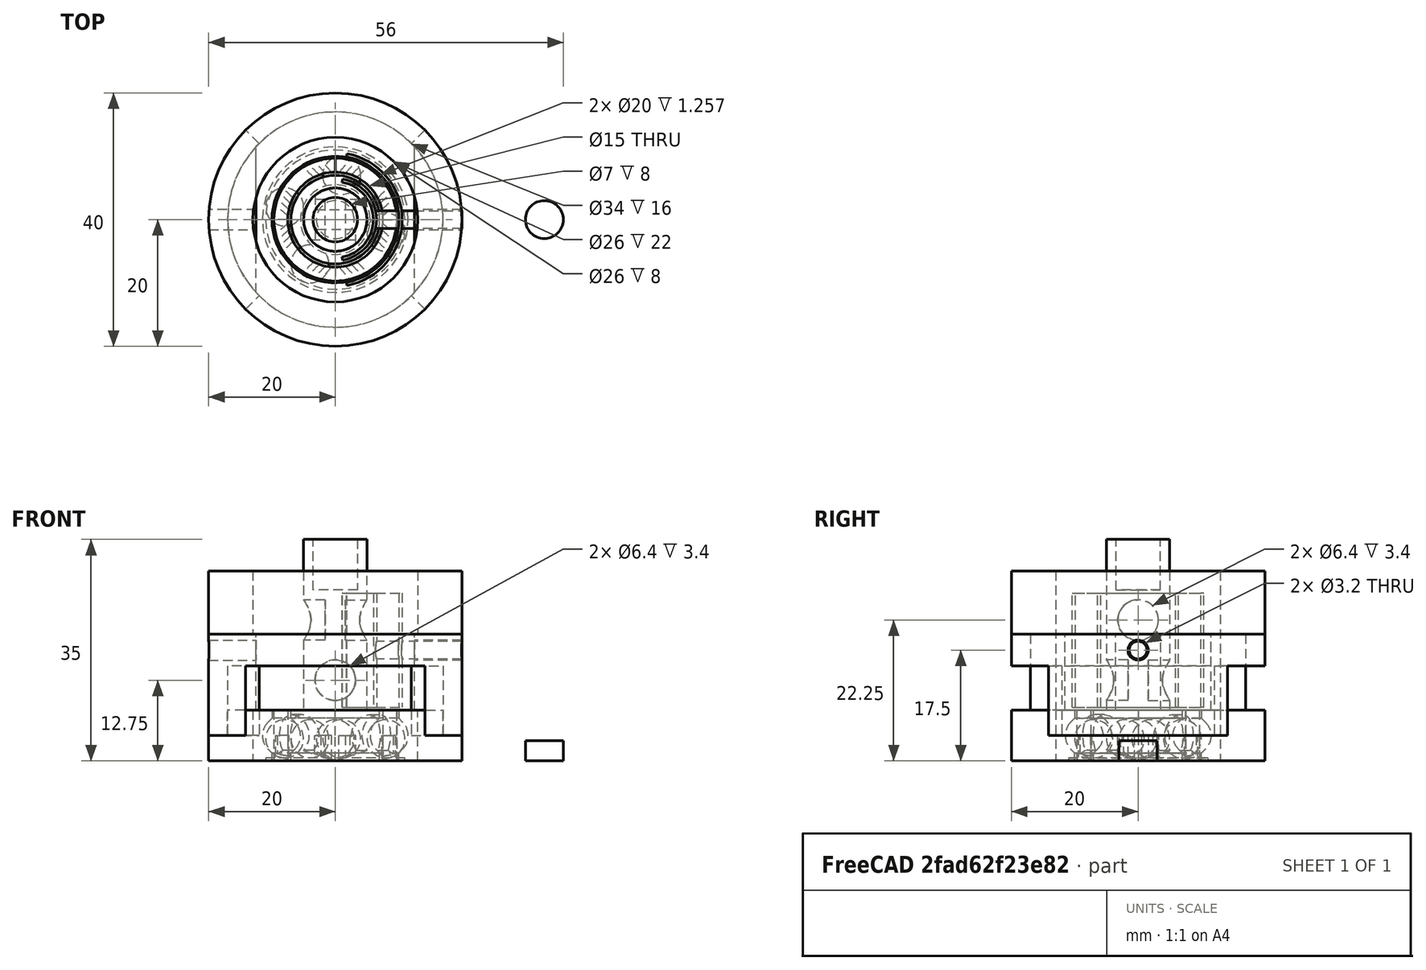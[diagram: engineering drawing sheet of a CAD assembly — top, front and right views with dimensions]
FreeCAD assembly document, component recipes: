
FREECAD ASSEMBLY — COMPONENT RECIPES ("laser")

This assembly document has 11 components, labeled P0..P10 below (a component is one placed body or linked part). 6 of them carry a construction recipe — the FreeCAD feature program that regenerates the part from scratch, quoted from this document or its linked companion documents; the rest are supplied as boundary geometry only. No exploded tour is included for this assembly.
COMPONENT P0 — recipe-attached ("bearing_body001", modeled in this document).
Construction recipe (the document's own serialized feature program — sketch geometry with constraints, then the solid features built on it; lengths are millimeters unless a unit is written):

FEATURE [PartDesign::SubShapeBinder] Binder
  BindCopyOnChange = 0
  BindMode = 0
  ClaimChildren = false
  Context = -> Body007 [Binder.]
  Fuse = false
  MakeFace = true
  OffsetFill = false
  OffsetIntersection = false
  OffsetJoinType = 0
  OffsetOpenResult = false
  PartialLoad = false
  Refine = true
  Relative = true
  Support = -> [Body[Revolution.]]
  _Version = 2
FEATURE [Sketcher::SketchObject] Sketch035
  ArcFitTolerance = 1e-06
  AttachmentSupport = -> [XZ_Plane008]
  ExternalGeometry = -> [Binder]
  ExternalTypes = [0]
  FullyConstrained = true
  MakeInternals = false
  MapMode = 5
  Placement = pos=(0,0,0) rot=(1,0,0;1.5708rad)
  expr: Constraints[25] = Spreadsheet.bearing_ball_radius
  expr: Constraints[6] = Spreadsheet.bearing_ball_radius + Spreadsheet.bearing_ball_radius_extra_play / 2
  sketch-geometry (17):
    g0: LineSegment [constr] StartX=8.5 StartY=8 StartZ=0 EndX=8.5 EndY=0 EndZ=0
    g1: LineSegment StartX=10 StartY=8 StartZ=0 EndX=10 EndY=6.74264 EndZ=0
    g2: LineSegment [constr] StartX=7 StartY=6.74264 StartZ=0 EndX=10 EndY=6.74264 EndZ=0
    g3: GeomPoint [constr] X=8.5 Y=4 Z=0
    g4: ArcOfCircle CenterX=8.5 CenterY=4 CenterZ=0 NormalX=0 NormalY=0 NormalZ=1 AngleXU=0 Radius=3 StartAngle=0 EndAngle=0.785398
    g5: LineSegment StartX=10.6213 StartY=6.12132 StartZ=0 EndX=10 EndY=6.74264 EndZ=0
    g6: ArcOfCircle CenterX=8.5 CenterY=4 CenterZ=0 NormalX=0 NormalY=0 NormalZ=1 AngleXU=0 Radius=3 StartAngle=5.49779 EndAngle=6.28319
    g7: LineSegment StartX=10 StartY=0 StartZ=0 EndX=10 EndY=1.25736 EndZ=0
    g8: LineSegment StartX=10.6213 StartY=1.87868 StartZ=0 EndX=10 EndY=1.25736 EndZ=0
    g9: LineSegment [constr] StartX=8.5 StartY=4 StartZ=0 EndX=11.5 EndY=4 EndZ=0
    g10: LineSegment StartX=10 StartY=8 StartZ=0 EndX=13 EndY=8 EndZ=0
    g11: LineSegment [constr] StartX=7 StartY=8 StartZ=0 EndX=10 EndY=8 EndZ=0
    g12: LineSegment [constr] StartX=7 StartY=1.25736 StartZ=0 EndX=10 EndY=1.25736 EndZ=0
    g13: LineSegment StartX=13 StartY=8 StartZ=0 EndX=13 EndY=0 EndZ=0
    g14: LineSegment StartX=13 StartY=0 StartZ=0 EndX=10 EndY=0 EndZ=0
    g15: LineSegment [constr] StartX=0 StartY=0 StartZ=0 EndX=13 EndY=0 EndZ=0
    g16: LineSegment [constr] StartX=10 StartY=6.74264 StartZ=0 EndX=10 EndY=1.25736 EndZ=0
  constraints (43):
    c: Vertical(g0)
    c: Vertical(g1)
    c: Coincident(g2,g1)
    c: Horizontal(g2)
    c: Symmetric(g0,g0,g3)
    c: PointOnObject(g0,g-1)
    c: Radius(g4) = 3
    c: Angle(g4) = 0.785398
    c: Coincident(g4,g3)
    c: Coincident(g5,g1)
    c: Angle(g6) = 0.785398
    c: Coincident(g6,g3)
    c: Coincident(g6,g4)
    c: PointOnObject(g7,g-1)
    c: Coincident(g8,g7)
    c: Vertical(g7)
    c: Coincident(g9,g3)
    c: Coincident(g9,g4)
    c: Horizontal(g9)
    c: Horizontal(g10)
    c: Tangent(g5,g4) = -1.5708
    c: Tangent(g8,g6) = 1.5708
    c: Coincident(g1,g10)
    c: Coincident(g11,g1)
    c: Horizontal(g11)
    c: Distance(g11) = 3
    c: Coincident(g12,g7)
    c: Horizontal(g12)
    c: Equal(g12,g11)
    c: Coincident(g13,g10)
    c: PointOnObject(g13,g-1)
    c: Vertical(g13)
    c: Coincident(g14,g13)
    c: Coincident(g14,g7)
    c: Coincident(g15,g-1)
    c: Coincident(g15,g13)
    c: DistanceX(g15,g15) = 13
    c: Coincident(g16,g1)
    c: Coincident(g16,g7)
    c: Vertical(g16)
    c: PointOnObject(g0,g11)
    c: Coincident(g11,g-4)
    c: Coincident(g2,g-5)
FEATURE [PartDesign::Revolution] Revolution001
  Angle = 360
  Angle2 = 60
  Axis = (0,2e-16,1)
  Base = (0,0,0)
  FuseOrder = 1
  Placement = pos=(0,0,0) rot=(1,0,0;1.5708rad)
  Profile = -> Sketch035
  ReferenceAxis = -> Sketch035 [V_Axis]
  Refine = true
  Reversed = true
  Suppressed = false
  Type = 0
FEATURE [PartDesign::Body] Body007  label="bearing_body"
  AllowCompound = false
  Group = -> [Sketch035,Revolution001,Binder]
  Origin = -> Origin008
  Tip = -> Revolution001
COMPONENT P1 — recipe-attached ("bearing_holder001", modeled in this document).
Construction recipe (the document's own serialized feature program — sketch geometry with constraints, then the solid features built on it; lengths are millimeters unless a unit is written):

FEATURE [Sketcher::SketchObject] Sketch041
  ArcFitTolerance = 1e-06
  AttachmentSupport = -> [XY_Plane012]
  ExternalTypes = [0]
  FullyConstrained = true
  MakeInternals = false
  MapMode = 5
  sketch-geometry (2):
    g0: Circle CenterX=0 CenterY=0 CenterZ=0 NormalX=0 NormalY=0 NormalZ=1 AngleXU=0 Radius=13
    g1: Circle CenterX=0 CenterY=0 CenterZ=0 NormalX=0 NormalY=0 NormalZ=1 AngleXU=0 Radius=20
  constraints (4):
    c: Diameter(g0) = 26
    c: Coincident(g0,g-1)
    c: Diameter(g1) = 40
    c: Coincident(g1,g0)
FEATURE [PartDesign::Pad] Pad018
  Direction = (0,0,1)
  Length = 8
  Length2 = 10
  Profile = -> Sketch041
  ReferenceAxis = -> Sketch041 [N_Axis]
  Refine = true
  SideType = 0
  Suppressed = false
  Type = 0
  Type2 = 0
FEATURE [Sketcher::SketchObject] Sketch042
  ArcFitTolerance = 1e-06
  AttachmentSupport = -> [Pad018]
  ExternalGeometry = -> [Pad018]
  ExternalTypes = [0]
  FullyConstrained = true
  MakeInternals = false
  MapMode = 5
  Placement = pos=(0,0,8) rot=(0,0,1;0rad)
  sketch-geometry (10):
    g0: ArcOfCircle CenterX=0 CenterY=0 CenterZ=0 NormalX=0 NormalY=0 NormalZ=1 AngleXU=0 Radius=20 StartAngle=5.49779 EndAngle=7.06858
    g1: ArcOfCircle CenterX=0 CenterY=0 CenterZ=0 NormalX=0 NormalY=0 NormalZ=1 AngleXU=0 Radius=17 StartAngle=5.49779 EndAngle=7.06858
    g2: LineSegment StartX=12.0208 StartY=-12.0208 StartZ=0 EndX=14.1421 EndY=-14.1421 EndZ=0
    g3: LineSegment StartX=12.0208 StartY=12.0208 StartZ=0 EndX=14.1421 EndY=14.1421 EndZ=0
    g4: LineSegment [constr] StartX=0 StartY=0 StartZ=0 EndX=12.0208 EndY=12.0208 EndZ=0
    g5: ArcOfCircle CenterX=0 CenterY=0 CenterZ=0 NormalX=0 NormalY=0 NormalZ=1 AngleXU=0 Radius=20 StartAngle=2.35619 EndAngle=3.92699
    g6: ArcOfCircle CenterX=0 CenterY=0 CenterZ=0 NormalX=0 NormalY=0 NormalZ=1 AngleXU=0 Radius=17 StartAngle=2.35619 EndAngle=3.92699
    g7: LineSegment [constr] StartX=0 StartY=0 StartZ=0 EndX=-12.0208 EndY=-12.0208 EndZ=0
    g8: LineSegment StartX=-12.0208 StartY=12.0208 StartZ=0 EndX=-14.1421 EndY=14.1421 EndZ=0
    g9: LineSegment StartX=-12.0208 StartY=-12.0208 StartZ=0 EndX=-14.1421 EndY=-14.1421 EndZ=0
  constraints (28):
    c: Angle(g0) = 1.5708
    c: Coincident(g0,g-1)
    c: PointOnObject(g0,g-3)
    c: Angle(g1) = 1.5708
    c: Coincident(g1,g0)
    c: Coincident(g2,g1)
    c: Coincident(g2,g0)
    c: Coincident(g3,g1)
    c: Coincident(g3,g0)
    c: Distance(g3) = 3
    c: Coincident(g4,g0)
    c: Coincident(g4,g1)
    c: Parallel(g3,g4)
    c: Angle(g-1,g4) = 0.785398
    c: Angle(g5) = 1.5708
    c: Coincident(g5,g0)
    c: PointOnObject(g5,g-3)
    c: Angle(g6) = 1.5708
    c: Coincident(g6,g0)
    c: Coincident(g7,g0)
    c: Coincident(g7,g6)
    c: Angle(g7,g-1) = 2.35619
    c: Coincident(g8,g6)
    c: Coincident(g8,g5)
    c: Coincident(g9,g6)
    c: Coincident(g9,g5)
    c: Distance(g8) = 3
    c: Parallel(g9,g7)
FEATURE [PartDesign::Pocket] Pocket018
  BaseFeature = -> Pad018
  Direction = (0,0,-1)
  Length = 4
  Length2 = 5
  Profile = -> Sketch042
  ReferenceAxis = -> Sketch042 [N_Axis]
  Refine = true
  SideType = 0
  Suppressed = false
  Type = 0
  Type2 = 0
FEATURE [PartDesign::Body] Body011  label="bearing_holder"
  AllowCompound = false
  Group = -> [Sketch041,Pad018,Sketch042,Pocket018]
  Origin = -> Origin012
  Tip = -> Pocket018
COMPONENT P2 — recipe-attached ("coil001", modeled in this document).
Construction recipe (the document's own serialized feature program — sketch geometry with constraints, then the solid features built on it; lengths are millimeters unless a unit is written):

FEATURE [Sketcher::SketchObject] Sketch046
  ArcFitTolerance = 1e-06
  AttachmentOffset = pos=(0,0,8.5) rot=(0,0,1;0rad)
  AttachmentSupport = -> [XY_Plane014]
  ExternalTypes = [0]
  FullyConstrained = true
  MakeInternals = false
  MapMode = 5
  Placement = pos=(0,0,8.5) rot=(0,0,1;0rad)
  sketch-geometry (11):
    g0: GeomPoint X=5 Y=0 Z=0
    g1: GeomPoint X=6 Y=0 Z=0
    g2: LineSegment [constr] StartX=5 StartY=0 StartZ=0 EndX=6 EndY=0 EndZ=0
    g3: LineSegment [constr] StartX=1.04189 StartY=5.90885 StartZ=0 EndX=1.12871 EndY=6.40125 EndZ=0
    g4: ArcOfCircle CenterX=0 CenterY=0 CenterZ=0 NormalX=0 NormalY=0 NormalZ=1 AngleXU=0 Radius=6 StartAngle=4.88692 EndAngle=7.67945
    g5: LineSegment [constr] StartX=1.04189 StartY=-5.90885 StartZ=0 EndX=0 EndY=0 EndZ=0
    g6: LineSegment [constr] StartX=0 StartY=0 StartZ=0 EndX=1.04189 EndY=5.90885 EndZ=0
    g7: ArcOfCircle CenterX=0 CenterY=0 CenterZ=0 NormalX=0 NormalY=0 NormalZ=1 AngleXU=0 Radius=6.5 StartAngle=4.88692 EndAngle=7.67945
    g8: LineSegment [constr] StartX=1.12871 StartY=-6.40125 StartZ=0 EndX=1.04189 EndY=-5.90885 EndZ=0
    g9: LineSegment StartX=1.12871 StartY=-6.40125 StartZ=0 EndX=1.04189 EndY=-5.90885 EndZ=0
    g10: LineSegment StartX=1.12871 StartY=6.40125 StartZ=0 EndX=1.04189 EndY=5.90885 EndZ=0
  constraints (26):
    c: PointOnObject(g0,g-3)
    c: PointOnObject(g1,g4)
    c: PointOnObject(g0,g-1)
    c: PointOnObject(g1,g-1)
    c: Coincident(g2,g0)
    c: Coincident(g2,g1)
    c: Distance(g2,g2) = 1
    c: Coincident(g5,g-1)
    c: Angle(g-1,g6) = 1.39626
    c: Angle(g5,g-1) = 1.39626
    c: Coincident(g6,g4)
    c: Coincident(g4,g5)
    c: Coincident(g7,g4)
    c: Parallel(g3,g6)
    c: Coincident(g3,g7)
    c: Coincident(g6,g4)
    c: Coincident(g3,g4)
    c: Distance(g3,g3) = 0.5
    c: Coincident(g8,g7)
    c: Coincident(g8,g4)
    c: Parallel(g8,g5)
    c: Coincident(g4,g5)
    c: Coincident(g9,g7)
    c: Coincident(g9,g4)
    c: Coincident(g10,g3)
    c: Coincident(g10,g3)
FEATURE [PartDesign::SubShapeBinder] Binder011
  BindCopyOnChange = 0
  BindMode = 0
  ClaimChildren = false
  Context = -> Body013 [Binder011.]
  Fuse = false
  MakeFace = true
  OffsetFill = false
  OffsetIntersection = false
  OffsetJoinType = 0
  OffsetOpenResult = false
  PartialLoad = false
  Refine = true
  Relative = true
  Support = -> [Body]
  _Version = 2
FEATURE [PartDesign::Pad] Pad023
  Direction = (0,0,1)
  Length = 18
  Length2 = 10
  Profile = -> Sketch046
  ReferenceAxis = -> Sketch046 [N_Axis]
  Refine = true
  SideType = 0
  Suppressed = false
  Type = 0
  Type2 = 0
FEATURE [Sketcher::SketchObject] Sketch047
  ArcFitTolerance = 1e-06
  AttachmentSupport = -> [Pad023]
  ExternalGeometry = -> [Pad023]
  ExternalTypes = [0]
  FullyConstrained = true
  MakeInternals = false
  MapMode = 5
  Placement = pos=(0,0,26.5) rot=(0,0,1;0rad)
  sketch-geometry (3):
    g0: GeomPoint X=6.5 Y=0 Z=0
    g1: GeomPoint X=6 Y=0 Z=0
    g2: LineSegment StartX=6 StartY=0 StartZ=0 EndX=6.5 EndY=0 EndZ=0
  constraints (6):
    c: PointOnObject(g0,g-4)
    c: PointOnObject(g1,g-3)
    c: Coincident(g2,g1)
    c: Coincident(g2,g0)
    c: Horizontal(g2)
    c: PointOnObject(g0,g-1)
FEATURE [PartDesign::Plane] DatumPlane006
  AttachmentOffset = pos=(0,0,0) rot=(0,1,0;3.14159rad)
  AttachmentSupport = -> [Sketch047]
  Length = 60.1489
  MapMode = 7
  Placement = pos=(6.5,0,26.5) rot=(0.57735,0.57735,0.57735;2.0944rad)
  ResizeMode = 0
  Width = 61.6489
FEATURE [Sketcher::SketchObject] Sketch049
  ArcFitTolerance = 1e-06
  AttachmentOffset = pos=(0,0,-0.5) rot=(0,0,1;0rad)
  AttachmentSupport = -> [DatumPlane006]
  ExternalGeometry = -> [Pad023]
  ExternalTypes = [0]
  FullyConstrained = true
  MakeInternals = false
  MapMode = 5
  Placement = pos=(6,0,26.5) rot=(0.57735,0.57735,0.57735;2.0944rad)
  sketch-geometry (4):
    g0: LineSegment [constr] StartX=-6.40125 StartY=0 StartZ=0 EndX=6.40125 EndY=-18 EndZ=0
    g1: LineSegment [constr] StartX=-6.40125 StartY=-18 StartZ=0 EndX=6.40125 EndY=0 EndZ=0
    g2: GeomPoint [constr] X=0 Y=-9 Z=0
    g3: Circle CenterX=0 CenterY=-9 CenterZ=0 NormalX=0 NormalY=0 NormalZ=1 AngleXU=0 Radius=1.4
  constraints (7):
    c: Coincident(g0,g-5)
    c: Coincident(g0,g-6)
    c: Coincident(g1,g-6)
    c: Coincident(g1,g-5)
    c: Symmetric(g0,g0,g2)
    c: Diameter(g3) = 2.8
    c: Coincident(g3,g2)
FEATURE [PartDesign::Pad] Pad024
  BaseFeature = -> Pad023
  Direction = (1,0,0)
  Length = 14
  Length2 = 10
  Profile = -> Sketch049
  ReferenceAxis = -> Sketch049 [N_Axis]
  Refine = true
  SideType = 0
  Suppressed = false
  Type = 0
  Type2 = 0
FEATURE [Sketcher::SketchObject] Sketch050
  ArcFitTolerance = 1e-06
  AttachmentOffset = pos=(0,0,8.5) rot=(0,0,1;0rad)
  AttachmentSupport = -> [XY_Plane014]
  ExternalGeometry = -> [Pad023]
  ExternalTypes = [0]
  FullyConstrained = true
  MakeInternals = false
  MapMode = 5
  Placement = pos=(0,0,8.5) rot=(0,0,1;0rad)
  sketch-geometry (7):
    g0: ArcOfCircle CenterX=0 CenterY=0 CenterZ=0 NormalX=0 NormalY=0 NormalZ=1 AngleXU=0 Radius=10.054 StartAngle=4.88692 EndAngle=7.67945
    g1: LineSegment [constr] StartX=1.83268 StartY=-10.3937 StartZ=0 EndX=1.74586 EndY=-9.90125 EndZ=0
    g2: LineSegment StartX=1.83268 StartY=10.3937 StartZ=0 EndX=1.74586 EndY=9.90125 EndZ=0
    g3: LineSegment StartX=1.83268 StartY=-10.3937 StartZ=0 EndX=1.74586 EndY=-9.90125 EndZ=0
    g4: ArcOfCircle CenterX=0 CenterY=0 CenterZ=0 NormalX=0 NormalY=0 NormalZ=1 AngleXU=0 Radius=10.554 StartAngle=4.88692 EndAngle=7.67945
    g5: LineSegment [constr] StartX=1.74586 StartY=-9.90125 StartZ=0 EndX=1.12871 EndY=-6.40125 EndZ=0
    g6: LineSegment [constr] StartX=1.12871 StartY=6.40125 StartZ=0 EndX=1.74586 EndY=9.90125 EndZ=0
  constraints (18):
    c: Coincident(g1,g0)
    c: Coincident(g2,g0)
    c: Coincident(g3,g0)
    c: Coincident(g0,g-1)
    c: Coincident(g4,g0)
    c: Coincident(g4,g3)
    c: Coincident(g4,g2)
    c: Coincident(g1,g3)
    c: Parallel(g2,g-5)
    c: Parallel(g3,g-6)
    c: Coincident(g5,g0)
    c: Coincident(g5,g-6)
    c: Parallel(g-6,g5)
    c: Coincident(g6,g-5)
    c: Coincident(g6,g0)
    c: Parallel(g6,g-5)
    c: Distance(g2,g2) = 0.5
    c: DistanceY(g6,g6) = 3.5
FEATURE [PartDesign::Pad] Pad025
  BaseFeature = -> Pad024
  Direction = (0,0,1)
  Length = 18
  Length2 = 10
  Profile = -> Sketch050
  ReferenceAxis = -> Sketch050 [N_Axis]
  Refine = true
  SideType = 0
  Suppressed = false
  Type = 0
  Type2 = 0
FEATURE [PartDesign::Body] Body013  label="coil"
  AllowCompound = false
  Group = -> [Sketch046,Binder011,Pad023,Sketch047,DatumPlane006,Sketch049,Pad024,Sketch050,Pad025]
  Origin = -> Origin014
  Tip = -> Pad025
COMPONENT P3 — same part as P2; its construction recipe is shown at P2.
COMPONENT P4 — recipe-attached ("coil_frame001", modeled in this document).
Construction recipe (the document's own serialized feature program — sketch geometry with constraints, then the solid features built on it; lengths are millimeters unless a unit is written):

FEATURE [PartDesign::SubShapeBinder] Binder009
  BindCopyOnChange = 0
  BindMode = 0
  ClaimChildren = false
  Context = -> Body012 [Binder009.]
  Fuse = false
  MakeFace = true
  OffsetFill = false
  OffsetIntersection = false
  OffsetJoinType = 0
  OffsetOpenResult = false
  PartialLoad = false
  Refine = true
  Relative = true
  Support = -> [Body011]
  _Version = 2
FEATURE [Sketcher::SketchObject] Sketch044
  ArcFitTolerance = 1e-06
  AttachmentOffset = pos=(0,0,15) rot=(0,0,1;0rad)
  AttachmentSupport = -> [Binder009]
  ExternalTypes = [0]
  FullyConstrained = true
  MakeInternals = false
  MapMode = 5
  Placement = pos=(0,0,15) rot=(0,0,1;3.14159rad)
  sketch-geometry (15):
    g0: Circle CenterX=0 CenterY=0 CenterZ=0 NormalX=0 NormalY=0 NormalZ=1 AngleXU=0 Radius=20
    g1: Circle [constr] CenterX=0 CenterY=0 CenterZ=0 NormalX=0 NormalY=0 NormalZ=1 AngleXU=0 Radius=6.5
    g2: GeomPoint [constr] X=5 Y=0 Z=0
    g3: LineSegment [constr] StartX=6.5 StartY=0 StartZ=0 EndX=5 EndY=0 EndZ=0
    g4: LineSegment StartX=12.5 StartY=11.5217 StartZ=0 EndX=12.5 EndY=-11.5217 EndZ=0
    g5: ArcOfCircle CenterX=-1.6699e-12 CenterY=-6e-16 CenterZ=0 NormalX=0 NormalY=0 NormalZ=1 AngleXU=0 Radius=17 StartAngle=0.744696 EndAngle=2.3969
    g6: GeomPoint X=12.5 Y=0 Z=0
    g7: LineSegment StartX=-12.5 StartY=11.5217 StartZ=0 EndX=-12.5 EndY=-11.5217 EndZ=0
    g8: ArcOfCircle CenterX=0 CenterY=0 CenterZ=0 NormalX=0 NormalY=0 NormalZ=1 AngleXU=0 Radius=17 StartAngle=3.88629 EndAngle=5.53849
    g9: GeomPoint X=-12.5 Y=0 Z=0
    g10: GeomPoint X=-6.5 Y=0 Z=0
    g11: LineSegment [constr] StartX=-12.5 StartY=0 StartZ=0 EndX=-6.5 EndY=0 EndZ=0
    g12: LineSegment [constr] StartX=12.5 StartY=0 StartZ=0 EndX=6.5 EndY=0 EndZ=0
    g13: Circle [constr] CenterX=-1.6699e-12 CenterY=-6e-16 CenterZ=0 NormalX=0 NormalY=0 NormalZ=1 AngleXU=0 Radius=17
    g14: GeomPoint [constr] X=-12.0208 Y=-12.0208 Z=0
  constraints (35):
    c: Coincident(g0,g-1)
    c: Coincident(g1,g0)
    c: PointOnObject(g2,g-5)
    c: PointOnObject(g3,g1)
    c: Coincident(g3,g2)
    c: PointOnObject(g2,g-1)
    c: PointOnObject(g3,g-1)
    c: Distance(g3,g3) = 1.5
    c: PointOnObject(g4,g5)
    c: PointOnObject(g-3,g0)
    c: Coincident(g8,g4)
    c: PointOnObject(g5,g4)
    c: Symmetric(g4,g4,g6)
    c: PointOnObject(g6,g-1)
    c: PointOnObject(g9,g7)
    c: PointOnObject(g10,g1)
    c: PointOnObject(g10,g-1)
    c: PointOnObject(g9,g-1)
    c: Coincident(g11,g9)
    c: Coincident(g11,g10)
    c: Coincident(g12,g6)
    c: Coincident(g12,g3)
    c: Equal(g11,g12)
    c: Coincident(g7,g5)
    c: Coincident(g7,g8)
    c: Vertical(g7)
    c: Distance(g12,g12) = 6
    c: Vertical(g4)
    c: Equal(g4,g7)
    c: Coincident(g8,g0)
    c: Coincident(g13,g5)
    c: PointOnObject(g-4,g13)
    c: PointOnObject(g5,g13)
    c: PointOnObject(g14,g13)
    c: Coincident(g14,g-4)
FEATURE [PartDesign::Pad] Pad021
  Direction = (0,0,1)
  Length = 5
  Length2 = 10
  Profile = -> Sketch044
  ReferenceAxis = -> Sketch044 [N_Axis]
  Refine = true
  SideType = 0
  Suppressed = false
  Type = 0
  Type2 = 0
FEATURE [Sketcher::SketchObject] Sketch045
  ArcFitTolerance = 1e-06
  AttachmentSupport = -> [Pad021]
  ExternalGeometry = -> [Binder009]
  ExternalTypes = [0]
  FullyConstrained = true
  MakeInternals = false
  MapMode = 5
  Placement = pos=(0,0,15) rot=(1,0,0;3.14159rad)
  sketch-geometry (12):
    g0: ArcOfCircle CenterX=0 CenterY=0 CenterZ=0 NormalX=0 NormalY=0 NormalZ=1 AngleXU=0 Radius=20 StartAngle=2.35619 EndAngle=3.92699
    g1: ArcOfCircle CenterX=0 CenterY=0 CenterZ=0 NormalX=0 NormalY=0 NormalZ=1 AngleXU=0 Radius=17 StartAngle=2.35619 EndAngle=3.92699
    g2: ArcOfCircle CenterX=0 CenterY=0 CenterZ=0 NormalX=0 NormalY=0 NormalZ=1 AngleXU=0 Radius=20 StartAngle=5.49779 EndAngle=7.06858
    g3: ArcOfCircle CenterX=0 CenterY=0 CenterZ=0 NormalX=0 NormalY=0 NormalZ=1 AngleXU=0 Radius=17 StartAngle=5.49779 EndAngle=7.06858
    g4: LineSegment StartX=-14.1421 StartY=-14.1421 StartZ=0 EndX=-12.0208 EndY=-12.0208 EndZ=0
    g5: LineSegment StartX=-14.1421 StartY=14.1421 StartZ=0 EndX=-12.0208 EndY=12.0208 EndZ=0
    g6: LineSegment StartX=14.1421 StartY=-14.1421 StartZ=0 EndX=12.0208 EndY=-12.0208 EndZ=0
    g7: LineSegment StartX=14.1421 StartY=14.1421 StartZ=0 EndX=12.0208 EndY=12.0208 EndZ=0
    g8: LineSegment [constr] StartX=0 StartY=0 StartZ=0 EndX=12.0208 EndY=-12.0208 EndZ=0
    g9: LineSegment [constr] StartX=-12.0208 StartY=-12.0208 StartZ=0 EndX=0 EndY=0 EndZ=0
    g10: LineSegment [constr] StartX=12.0208 StartY=-12.0208 StartZ=0 EndX=14.1421 EndY=-14.1421 EndZ=0
    g11: LineSegment [constr] StartX=-14.1421 StartY=-14.1421 StartZ=0 EndX=-12.0208 EndY=-12.0208 EndZ=0
  constraints (28):
    c: Coincident(g0,g-1)
    c: Coincident(g0,g-4)
    c: Coincident(g1,g0)
    c: Coincident(g1,g-3)
    c: Coincident(g2,g0)
    c: Coincident(g2,g-7)
    c: Coincident(g3,g0)
    c: Coincident(g3,g-5)
    c: Coincident(g4,g0)
    c: Coincident(g4,g1)
    c: Coincident(g5,g0)
    c: Coincident(g5,g1)
    c: Coincident(g6,g2)
    c: Coincident(g6,g3)
    c: Coincident(g7,g2)
    c: Coincident(g7,g3)
    c: Coincident(g8,g0)
    c: Coincident(g8,g3)
    c: Coincident(g9,g1)
    c: Coincident(g9,g0)
    c: Parallel(g4,g9)
    c: Parallel(g8,g6)
    c: Coincident(g10,g-5)
    c: Coincident(g10,g-6)
    c: Parallel(g6,g10)
    c: Coincident(g11,g-4)
    c: Coincident(g11,g-3)
    c: Parallel(g4,g11)
FEATURE [PartDesign::Pad] Pad022
  BaseFeature = -> Pad021
  Direction = (0,0,-1)
  Length = 10
  Length2 = 10
  Profile = -> Sketch045
  ReferenceAxis = -> Sketch045 [N_Axis]
  Refine = true
  SideType = 0
  Suppressed = false
  Type = 3
  Type2 = 0
  UpToFace = -> Binder009 [Face7]
FEATURE [PartDesign::SubShapeBinder] Binder010
  BindCopyOnChange = 0
  BindMode = 0
  ClaimChildren = false
  Context = -> Body012 [Binder010.]
  Fuse = false
  MakeFace = true
  OffsetFill = false
  OffsetIntersection = false
  OffsetJoinType = 0
  OffsetOpenResult = false
  PartialLoad = false
  Refine = true
  Relative = true
  Support = -> [Body]
  _Version = 2
FEATURE [PartDesign::SubShapeBinder] Binder012
  BindCopyOnChange = 0
  BindMode = 0
  ClaimChildren = false
  Context = -> Body012 [Binder012.]
  Fuse = false
  MakeFace = true
  OffsetFill = false
  OffsetIntersection = false
  OffsetJoinType = 0
  OffsetOpenResult = false
  PartialLoad = false
  Refine = true
  Relative = true
  Support = -> [Body013]
  _Version = 2
FEATURE [Sketcher::SketchObject] Sketch051
  ArcFitTolerance = 1e-06
  AttachmentSupport = -> [Pad021]
  ExternalGeometry = -> [Binder012]
  ExternalTypes = [0]
  FullyConstrained = true
  MakeInternals = false
  MapMode = 5
  Placement = pos=(-12.5,0,0) rot=(0.57735,0.57735,0.57735;2.0944rad)
  sketch-geometry (3):
    g0: Circle CenterX=-5e-16 CenterY=17.5 CenterZ=0 NormalX=0 NormalY=0 NormalZ=1 AngleXU=0 Radius=1.6
    g1: GeomPoint [constr] X=0 Y=19.1 Z=0
    g2: GeomPoint [constr] X=0 Y=18.9 Z=0
  constraints (6):
    c: Coincident(g0,g-3)
    c: PointOnObject(g1,g0)
    c: PointOnObject(g2,g-3)
    c: PointOnObject(g2,g-2)
    c: PointOnObject(g1,g-2)
    c: Distance(g1,g2) = 0.2
FEATURE [PartDesign::Pocket] Pocket019
  BaseFeature = -> Pad022
  Direction = (-1,0,0)
  Length = 5
  Length2 = 5
  Profile = -> Sketch051
  ReferenceAxis = -> Sketch051 [N_Axis]
  Refine = true
  SideType = 0
  Suppressed = false
  Type = 1
  Type2 = 0
FEATURE [PartDesign::SubShapeBinder] Binder013
  BindCopyOnChange = 0
  BindMode = 0
  ClaimChildren = false
  Context = -> Body012 [Binder013.]
  Fuse = false
  MakeFace = true
  OffsetFill = false
  OffsetIntersection = false
  OffsetJoinType = 0
  OffsetOpenResult = false
  PartialLoad = false
  Placement = pos=(0,0,0) rot=(0,0,1;3.14159rad)
  Refine = true
  Relative = true
  Support = -> [Body013]
  _Version = 2
FEATURE [Sketcher::SketchObject] Sketch052
  ArcFitTolerance = 1e-06
  AttachmentSupport = -> [Pocket019]
  ExternalGeometry = -> [Binder013]
  ExternalTypes = [0]
  FullyConstrained = true
  MakeInternals = false
  MapMode = 5
  Placement = pos=(12.5,0,0) rot=(0.57735,-0.57735,-0.57735;2.0944rad)
  sketch-geometry (3):
    g0: Circle CenterX=3.4e-15 CenterY=17.5 CenterZ=0 NormalX=0 NormalY=0 NormalZ=1 AngleXU=0 Radius=1.6
    g1: GeomPoint X=0 Y=18.9 Z=0
    g2: GeomPoint [constr] X=0 Y=19.1 Z=0
  constraints (6):
    c: Coincident(g0,g-3)
    c: PointOnObject(g1,g-3)
    c: PointOnObject(g1,g-2)
    c: PointOnObject(g2,g0)
    c: PointOnObject(g2,g-2)
    c: Distance(g2,g1) = 0.2
FEATURE [PartDesign::Pocket] Pocket020
  BaseFeature = -> Pocket019
  Direction = (1,0,0)
  Length = 5
  Length2 = 5
  Profile = -> Sketch052
  ReferenceAxis = -> Sketch052 [N_Axis]
  Refine = true
  SideType = 0
  Suppressed = false
  Type = 1
  Type2 = 0
FEATURE [PartDesign::Body] Body012  label="coil_frame"
  AllowCompound = false
  Group = -> [Binder009,Binder010,Pad021,Sketch044,Sketch045,Pad022,Binder012,Sketch051,Pocket019,Binder013,Sketch052,Pocket020]
  Origin = -> Origin013
  Tip = -> Pocket020
COMPONENT P5 — geometry summary ("crown001"; no construction recipe available for this part):
  bounding box: 19.4 x 19.4 x 8.0 mm
  tessellated surface: 2,840 triangles
  volume: 488 mm^3 (16% of its bounding box)
  symmetry: 4-fold rotationally symmetric about the z axis; mirror-symmetric across its x mid-plane, y mid-plane
COMPONENT P6 — geometry summary ("magnet001"; no construction recipe available for this part):
  bounding box: 6.5 x 6.5 x 6.0 mm
  tessellated surface: 500 triangles
  volume: 90 mm^3 (36% of its bounding box)
  symmetry: mirror-symmetric across its z mid-plane
COMPONENT P7 — geometry summary ("magnet002"; no construction recipe available for this part):
  bounding box: 6.5 x 6.5 x 6.0 mm
  tessellated surface: 500 triangles
  volume: 90 mm^3 (36% of its bounding box)
  symmetry: mirror-symmetric across its z mid-plane
COMPONENT P8 — geometry summary ("magnet003"; no construction recipe available for this part):
  bounding box: 6.5 x 6.5 x 6.0 mm
  tessellated surface: 500 triangles
  volume: 90 mm^3 (36% of its bounding box)
  symmetry: mirror-symmetric across its z mid-plane
COMPONENT P9 — geometry summary ("magnet004"; no construction recipe available for this part):
  bounding box: 6.5 x 6.5 x 6.0 mm
  tessellated surface: 500 triangles
  volume: 90 mm^3 (36% of its bounding box)
  symmetry: 2-fold rotationally symmetric about the z axis; mirror-symmetric across its z mid-plane
COMPONENT P10 — recipe-attached ("rotor001", modeled in this document).
Construction recipe (the document's own serialized feature program — sketch geometry with constraints, then the solid features built on it; lengths are millimeters unless a unit is written):

FEATURE [Sketcher::SketchObject] Sketch
  ArcFitTolerance = 1e-06
  AttachmentSupport = -> [XY_Plane]
  ExternalTypes = [0]
  FullyConstrained = true
  MakeInternals = false
  MapMode = 5
  sketch-geometry (2):
    g0: Circle CenterX=0 CenterY=0 CenterZ=0 NormalX=0 NormalY=0 NormalZ=1 AngleXU=0 Radius=5
    g1: GeomPoint X=0 Y=0 Z=0
  constraints (3):
    c: Diameter(g0) = 10
    c: Coincident(g1,g-1)
    c: Coincident(g0,g1)
FEATURE [PartDesign::Pad] Pad
  Direction = (0,0,1)
  Length = 35
  Length2 = 10
  Profile = -> Sketch
  ReferenceAxis = -> Sketch [N_Axis]
  Refine = true
  SideType = 0
  Suppressed = false
  Type = 0
  Type2 = 0
FEATURE [Sketcher::SketchObject] Sketch019
  ArcFitTolerance = 1e-06
  ExternalTypes = [0]
  FullyConstrained = true
  MakeInternals = false
  MapMode = 5
  Placement = pos=(0,0,35) rot=(0,0,1;0rad)
  sketch-geometry (1):
    g0: Circle CenterX=0 CenterY=0 CenterZ=0 NormalX=0 NormalY=0 NormalZ=1 AngleXU=0 Radius=3.5
  constraints (2):
    c: Diameter(g0) = 7
    c: Coincident(g0,g-1)
FEATURE [PartDesign::Pocket] Pocket007
  BaseFeature = -> Pad
  Direction = (0,0,-1)
  Length = 8
  Length2 = 5
  Profile = -> Sketch019
  ReferenceAxis = -> Sketch019 [N_Axis]
  Refine = true
  SideType = 0
  Suppressed = false
  Type = 0
  Type2 = 0
FEATURE [Sketcher::SketchObject] Sketch031
  ArcFitTolerance = 1e-06
  AttachmentSupport = -> [Pocket007]
  ExternalGeometry = -> [Pad]
  ExternalTypes = [0]
  FullyConstrained = true
  MakeInternals = false
  MapMode = 5
  Placement = pos=(0,0,35) rot=(0,0,1;0rad)
  sketch-geometry (4):
    g0: LineSegment StartX=0 StartY=0 StartZ=0 EndX=3e-16 EndY=5 EndZ=0
    g1: LineSegment StartX=0 StartY=0 StartZ=0 EndX=-5 EndY=-1e-16 EndZ=0
    g2: LineSegment StartX=0 StartY=0 StartZ=0 EndX=5 EndY=0 EndZ=0
    g3: LineSegment StartX=0 StartY=0 StartZ=0 EndX=-3.305e-13 EndY=-5 EndZ=0
  constraints (12):
    c: Coincident(g0,g-1)
    c: PointOnObject(g0,g-3)
    c: Angle(g-1,g0) = 1.5708
    c: Coincident(g1,g0)
    c: PointOnObject(g1,g-3)
    c: Angle(g1,g-1) = 3.14159
    c: Coincident(g3,g2)
    c: Coincident(g2,g0)
    c: PointOnObject(g3,g-3)
    c: PointOnObject(g2,g-3)
    c: Angle(g-1,g2) = 0
    c: Angle(g3,g-1) = 1.5708
FEATURE [PartDesign::Plane] DatumPlane  label="p2"
  AttachmentOffset = pos=(0,0,0) rot=(0,1,0;3.14159rad)
  AttachmentSupport = -> [Sketch031]
  Length = 60.9545
  MapMode = 7
  Placement = pos=(3e-16,5,35) rot=(0,0.707107,0.707107;3.14159rad)
  ResizeMode = 0
  Width = 70.9545
FEATURE [PartDesign::Plane] DatumPlane003  label="p3"
  AttachmentOffset = pos=(0,0,0) rot=(0,1,0;3.14159rad)
  AttachmentSupport = -> [Sketch031]
  Length = 60.9545
  MapMode = 7
  Placement = pos=(-5,-1e-16,35) rot=(-0.57735,0.57735,0.57735;4.18879rad)
  ResizeMode = 0
  Width = 70.9545
FEATURE [PartDesign::Plane] DatumPlane004  label="p4"
  AttachmentOffset = pos=(0,0,0) rot=(0,1,0;3.14159rad)
  AttachmentSupport = -> [Sketch031]
  Length = 60.9545
  MapMode = 7
  Placement = pos=(5,0,35) rot=(0.57735,0.57735,0.57735;2.0944rad)
  ResizeMode = 0
  Width = 70.9545
FEATURE [PartDesign::Plane] DatumPlane002  label="p1"
  AttachmentOffset = pos=(0,0,0) rot=(0,1,0;3.14159rad)
  AttachmentSupport = -> [Sketch031]
  Length = 60.9545
  MapMode = 7
  Placement = pos=(-3.305e-13,-5,35) rot=(-1,0,0;4.71239rad)
  ResizeMode = 0
  Width = 70.9545
FEATURE [Sketcher::SketchObject] Sketch034
  ArcFitTolerance = 1e-06
  AttachmentSupport = -> [XZ_Plane]
  ExternalTypes = [0]
  FullyConstrained = true
  MakeInternals = false
  MapMode = 5
  Placement = pos=(0,0,0) rot=(1,0,0;1.5708rad)
  expr: Constraints[13] = Spreadsheet.bearing_ball_radius
  expr: Constraints[38] = Spreadsheet.bearing_ball_radius + Spreadsheet.bearing_ball_radius_extra_play / 2
  sketch-geometry (20):
    g0: ArcOfCircle CenterX=8.5 CenterY=4 CenterZ=0 NormalX=0 NormalY=0 NormalZ=1 AngleXU=0 Radius=3 StartAngle=2.35619 EndAngle=3.14159
    g1: LineSegment StartX=6.37868 StartY=6.12132 StartZ=0 EndX=7 EndY=6.74264 EndZ=0
    g2: LineSegment StartX=7 StartY=6.74264 StartZ=0 EndX=7 EndY=8 EndZ=0
    g3: LineSegment StartX=7 StartY=8 StartZ=0 EndX=0 EndY=8 EndZ=0
    g4: LineSegment StartX=0 StartY=0 StartZ=0 EndX=7 EndY=0 EndZ=0
    g5: GeomPoint [constr] X=8.5 Y=4 Z=0
    g6: ArcOfCircle CenterX=8.5 CenterY=4 CenterZ=0 NormalX=0 NormalY=0 NormalZ=1 AngleXU=0 Radius=3 StartAngle=3.14159 EndAngle=3.92699
    g7: LineSegment StartX=6.37868 StartY=1.87868 StartZ=0 EndX=7 EndY=1.25736 EndZ=0
    g8: LineSegment StartX=7 StartY=0 StartZ=0 EndX=7 EndY=1.25736 EndZ=0
    g9: LineSegment [constr] StartX=7 StartY=6.74264 StartZ=0 EndX=10 EndY=6.74264 EndZ=0
    g10: GeomPoint [constr] X=8.5 Y=6.74264 Z=0
    g11: LineSegment [constr] StartX=8.5 StartY=6.74264 StartZ=0 EndX=8.5 EndY=0 EndZ=0
    g12: GeomPoint [constr] X=8.5 Y=4 Z=0
    g13: LineSegment [constr] StartX=8.5 StartY=4 StartZ=0 EndX=5 EndY=4 EndZ=0
    g14: LineSegment [constr] StartX=5 StartY=0 StartZ=0 EndX=5 EndY=8 EndZ=0
    g15: GeomPoint [constr] X=5 Y=4 Z=0
    g16: LineSegment StartX=0 StartY=8 StartZ=0 EndX=0 EndY=0 EndZ=0
    g17: LineSegment [constr] StartX=5.5 StartY=4 StartZ=0 EndX=8.5 EndY=4 EndZ=0
    g18: LineSegment [constr] StartX=7 StartY=6.74264 StartZ=0 EndX=7 EndY=1.25736 EndZ=0
    g19: LineSegment [constr] StartX=5.5 StartY=4 StartZ=0 EndX=5 EndY=4 EndZ=0
  constraints (46):
    c: Angle(g-1,g1) = 0.785398
    c: Tangent(g1,g0) = 1.5708
    c: Vertical(g2)
    c: Coincident(g2,g1)
    c: Horizontal(g3)
    c: Coincident(g3,g2)
    c: PointOnObject(g4,g-1)
    c: Coincident(g0,g5)
    c: Coincident(g6,g0)
    c: Angle(g-1,g7) = -0.785398
    c: Tangent(g7,g6) = -1.5708
    c: Coincident(g8,g4)
    c: Coincident(g7,g8)
    c: Distance(g9) = 3
    c: Horizontal(g9)
    c: Coincident(g9,g1)
    c: Symmetric(g9,g9,g10)
    c: Coincident(g11,g10)
    c: PointOnObject(g11,g-1)
    c: Vertical(g11)
    c: PointOnObject(g12,g11)
    c: Vertical(g8)
    c: Coincident(g0,g12)
    c: Coincident(g13,g0)
    c: Equal(g8,g2)
    c: Horizontal(g13)
    c: PointOnObject(g3,g-2)
    c: Coincident(g4,g-1)
    c: Vertical(g14)
    c: Coincident(g14,g-3)
    c: PointOnObject(g14,g3)
    c: Symmetric(g14,g14,g15)
    c: Coincident(g16,g3)
    c: Coincident(g16,g4)
    c: Coincident(g6,g0)
    c: PointOnObject(g0,g13)
    c: Coincident(g17,g0)
    c: Coincident(g17,g0)
    c: Distance(g17) = 3
    c: Coincident(g18,g1)
    c: Coincident(g18,g7)
    c: Coincident(g19,g0)
    c: Coincident(g19,g15)
    c: Distance(g19) = 0.5
    c: Coincident(g13,g15)
    c: Distance(g16,g16) = 8
FEATURE [PartDesign::Revolution] Revolution
  Angle = 360
  Angle2 = 60
  Axis = (0,2e-16,1)
  Base = (0,0,0)
  BaseFeature = -> Pocket007
  FuseOrder = 1
  Profile = -> Sketch034
  ReferenceAxis = -> Sketch034 [V_Axis]
  Refine = true
  Reversed = true
  Suppressed = false
  Type = 0
FEATURE [Sketcher::SketchObject] Sketch038
  ArcFitTolerance = 1e-06
  AttachmentSupport = -> [Revolution]
  ExternalGeometry = -> [Revolution]
  ExternalTypes = [0]
  FullyConstrained = true
  MakeInternals = false
  MapMode = 5
  Placement = pos=(0,0,35) rot=(0,0,1;0rad)
  sketch-geometry (3):
    g0: Circle CenterX=0 CenterY=0 CenterZ=0 NormalX=0 NormalY=0 NormalZ=1 AngleXU=0 Radius=5
    g1: GeomPoint X=5 Y=0 Z=0
    g2: Circle [constr] CenterX=0 CenterY=0 CenterZ=0 NormalX=0 NormalY=0 NormalZ=1 AngleXU=0 Radius=5
  constraints (6):
    c: Coincident(g0,g-1)
    c: PointOnObject(g1,g0)
    c: PointOnObject(g1,g-1)
    c: Coincident(g2,g0)
    c: PointOnObject(g1,g2)
    c: PointOnObject(g1,g-3)
FEATURE [Sketcher::SketchObject] Sketch053
  ArcFitTolerance = 1e-06
  AttachmentSupport = -> [Revolution]
  ExternalGeometry = -> [Revolution]
  ExternalTypes = [0]
  FullyConstrained = true
  MakeInternals = false
  MapMode = 5
  Placement = pos=(0,0,35) rot=(0,0,1;0rad)
  sketch-geometry (4):
    g0: Circle CenterX=0 CenterY=0 CenterZ=0 NormalX=0 NormalY=0 NormalZ=1 AngleXU=0 Radius=5
    g1: Circle CenterX=0 CenterY=0 CenterZ=0 NormalX=0 NormalY=0 NormalZ=1 AngleXU=0 Radius=8.5
    g2: GeomPoint X=5 Y=0 Z=0
    g3: GeomPoint X=5 Y=0 Z=0
  constraints (7):
    c: Coincident(g0,g-1)
    c: Diameter(g1) = 17
    c: Coincident(g1,g0)
    c: PointOnObject(g2,g-3)
    c: PointOnObject(g3,g0)
    c: PointOnObject(g3,g-1)
    c: Coincident(g3,g2)
FEATURE [Sketcher::SketchObject] Sketch066
  ArcFitTolerance = 1e-06
  AttachmentSupport = -> [DatumPlane004]
  ExternalGeometry = -> [Revolution]
  ExternalTypes = [0]
  FullyConstrained = true
  MakeInternals = false
  MapMode = 5
  Placement = pos=(5,0,35) rot=(0.57735,0.57735,0.57735;2.0944rad)
  sketch-geometry (7):
    g0: LineSegment [constr] StartX=-3.5 StartY=-8 StartZ=0 EndX=-3.5 EndY=-27 EndZ=0
    g1: LineSegment [constr] StartX=3.5 StartY=-8 StartZ=0 EndX=3.5 EndY=-27 EndZ=0
    g2: LineSegment [constr] StartX=-3.5 StartY=-17.5 StartZ=0 EndX=3.5 EndY=-17.5 EndZ=0
    g3: GeomPoint [constr] X=1e-16 Y=-17.5 Z=0
    g4: LineSegment [constr] StartX=1e-16 StartY=-17.5 StartZ=0 EndX=0 EndY=-8 EndZ=0
    g5: LineSegment [constr] StartX=1e-16 StartY=-17.5 StartZ=0 EndX=-7e-16 EndY=-27 EndZ=0
    g6: Circle CenterX=0 CenterY=-12.75 CenterZ=0 NormalX=0 NormalY=0 NormalZ=1 AngleXU=0 Radius=3.2
  constraints (15):
    c: Coincident(g0,g-3)
    c: PointOnObject(g0,g-4)
    c: Vertical(g0)
    c: Coincident(g1,g-3)
    c: PointOnObject(g1,g-4)
    c: Vertical(g1)
    c: Symmetric(g0,g0,g2)
    c: Symmetric(g1,g1,g2)
    c: Symmetric(g2,g2,g3)
    c: Coincident(g4,g3)
    c: Symmetric(g-3,g-3,g4)
    c: Coincident(g5,g3)
    c: Symmetric(g-4,g-4,g5)
    c: Diameter(g6) = 6.4
    c: Symmetric(g4,g4,g6)
FEATURE [PartDesign::Pocket] Pocket
  BaseFeature = -> Revolution
  Direction = (-1,0,0)
  Length = 3.4
  Length2 = 5
  Profile = -> Sketch066
  ReferenceAxis = -> Sketch066 [N_Axis]
  Refine = true
  SideType = 0
  Suppressed = false
  Type = 0
  Type2 = 0
FEATURE [Sketcher::SketchObject] Sketch067
  ArcFitTolerance = 1e-06
  AttachmentSupport = -> [DatumPlane]
  ExternalGeometry = -> [Pocket]
  ExternalTypes = [0]
  FullyConstrained = true
  MakeInternals = false
  MapMode = 5
  Placement = pos=(3e-16,5,35) rot=(0,0.707107,0.707107;3.14159rad)
  sketch-geometry (6):
    g0: LineSegment [constr] StartX=-3.5 StartY=-8 StartZ=0 EndX=-3.5 EndY=-27 EndZ=0
    g1: LineSegment [constr] StartX=3.5 StartY=-27 StartZ=0 EndX=3.5 EndY=-8 EndZ=0
    g2: LineSegment [constr] StartX=-3.5 StartY=-17.5 StartZ=0 EndX=3.5 EndY=-17.5 EndZ=0
    g3: LineSegment [constr] StartX=5e-16 StartY=-17.5 StartZ=0 EndX=0 EndY=-8 EndZ=0
    g4: LineSegment [constr] StartX=5e-16 StartY=-17.5 StartZ=0 EndX=0 EndY=-27 EndZ=0
    g5: Circle CenterX=3e-16 CenterY=-22.25 CenterZ=0 NormalX=0 NormalY=0 NormalZ=1 AngleXU=0 Radius=3.2
  constraints (14):
    c: Coincident(g0,g-4)
    c: PointOnObject(g0,g-3)
    c: PointOnObject(g1,g-3)
    c: Coincident(g1,g-4)
    c: Vertical(g1)
    c: Vertical(g0)
    c: Symmetric(g0,g0,g2)
    c: Symmetric(g1,g1,g2)
    c: Symmetric(g2,g2,g3)
    c: Symmetric(g-4,g-4,g3)
    c: Coincident(g4,g3)
    c: Symmetric(g-3,g-3,g4)
    c: Symmetric(g4,g4,g5)
    c: Diameter(g5) = 6.4
FEATURE [PartDesign::Pocket] Pocket025
  BaseFeature = -> Pocket
  Direction = (0,-1,2e-16)
  Length = 3.4
  Length2 = 5
  Profile = -> Sketch067
  ReferenceAxis = -> Sketch067 [N_Axis]
  Refine = true
  SideType = 0
  Suppressed = false
  Type = 0
  Type2 = 0
FEATURE [Sketcher::SketchObject] Sketch068
  ArcFitTolerance = 1e-06
  AttachmentSupport = -> [DatumPlane003]
  ExternalGeometry = -> [Pocket025]
  ExternalTypes = [0]
  FullyConstrained = true
  MakeInternals = false
  MapMode = 5
  Placement = pos=(-5,-1e-16,35) rot=(0.57735,-0.57735,-0.57735;2.0944rad)
  sketch-geometry (1):
    g0: Circle CenterX=0 CenterY=-12.75 CenterZ=0 NormalX=0 NormalY=0 NormalZ=1 AngleXU=0 Radius=3.2
  constraints (2):
    c: Coincident(g0,g-3)
    c: Equal(g0,g-3)
FEATURE [PartDesign::Pocket] Pocket026
  BaseFeature = -> Pocket025
  Direction = (1,0,0)
  Length = 3.4
  Length2 = 5
  Profile = -> Sketch068
  ReferenceAxis = -> Sketch068 [N_Axis]
  Refine = true
  SideType = 0
  Suppressed = false
  Type = 0
  Type2 = 0
FEATURE [Sketcher::SketchObject] Sketch069
  ArcFitTolerance = 1e-06
  AttachmentSupport = -> [DatumPlane002]
  ExternalGeometry = -> [Pocket026]
  ExternalTypes = [0]
  FullyConstrained = true
  MakeInternals = false
  MapMode = 5
  Placement = pos=(-3.305e-13,-5,35) rot=(1,0,0;1.5708rad)
  sketch-geometry (1):
    g0: Circle CenterX=0 CenterY=-22.25 CenterZ=0 NormalX=0 NormalY=0 NormalZ=1 AngleXU=0 Radius=3.2
  constraints (2):
    c: Coincident(g0,g-3)
    c: Equal(g0,g-3)
FEATURE [PartDesign::Pocket] Pocket027
  BaseFeature = -> Pocket026
  Direction = (6.62e-14,1,-2e-16)
  Length = 3.4
  Length2 = 5
  Profile = -> Sketch069
  ReferenceAxis = -> Sketch069 [N_Axis]
  Refine = true
  SideType = 0
  Suppressed = false
  Type = 0
  Type2 = 0
FEATURE [PartDesign::Pocket] Pocket021
  BaseFeature = -> Pocket027
  Direction = (0,0,-1)
  Length = 5
  Length2 = 5
  Profile = -> Sketch053
  ReferenceAxis = -> Sketch053 [N_Axis]
  Refine = true
  SideType = 0
  Suppressed = false
  Type = 1
  Type2 = 0
FEATURE [PartDesign::Pocket] Pocket016
  BaseFeature = -> Pocket021
  Direction = (0,0,-1)
  Length = 5
  Length2 = 5
  Profile = -> Sketch038
  ReferenceAxis = -> Sketch038 [N_Axis]
  Refine = true
  SideType = 0
  Suppressed = false
  Type = 1
  Type2 = 0
FEATURE [PartDesign::Body] Body  label="rotor"
  AllowCompound = false
  Group = -> [Sketch,Pad,Sketch019,Pocket007,Sketch031,DatumPlane002,DatumPlane,DatumPlane003,DatumPlane004,Sketch034,Revolution,Sketch066,Pocket,Sketch067,Pocket025,Sketch068,Pocket026,Sketch069,Pocket027,Pocket021,Pocket016,Sketch038,Sketch053]
  Origin = -> Origin
  Tip = -> Pocket027
PROVENANCE & LICENSES
A FreeCAD (.FCStd) document from a public repository crawl; recipes are the document's own serialized feature recipes (and, for linked parts, companion documents' recipes).
License: as declared in the source repository (recorded in the dataset sidecar).
